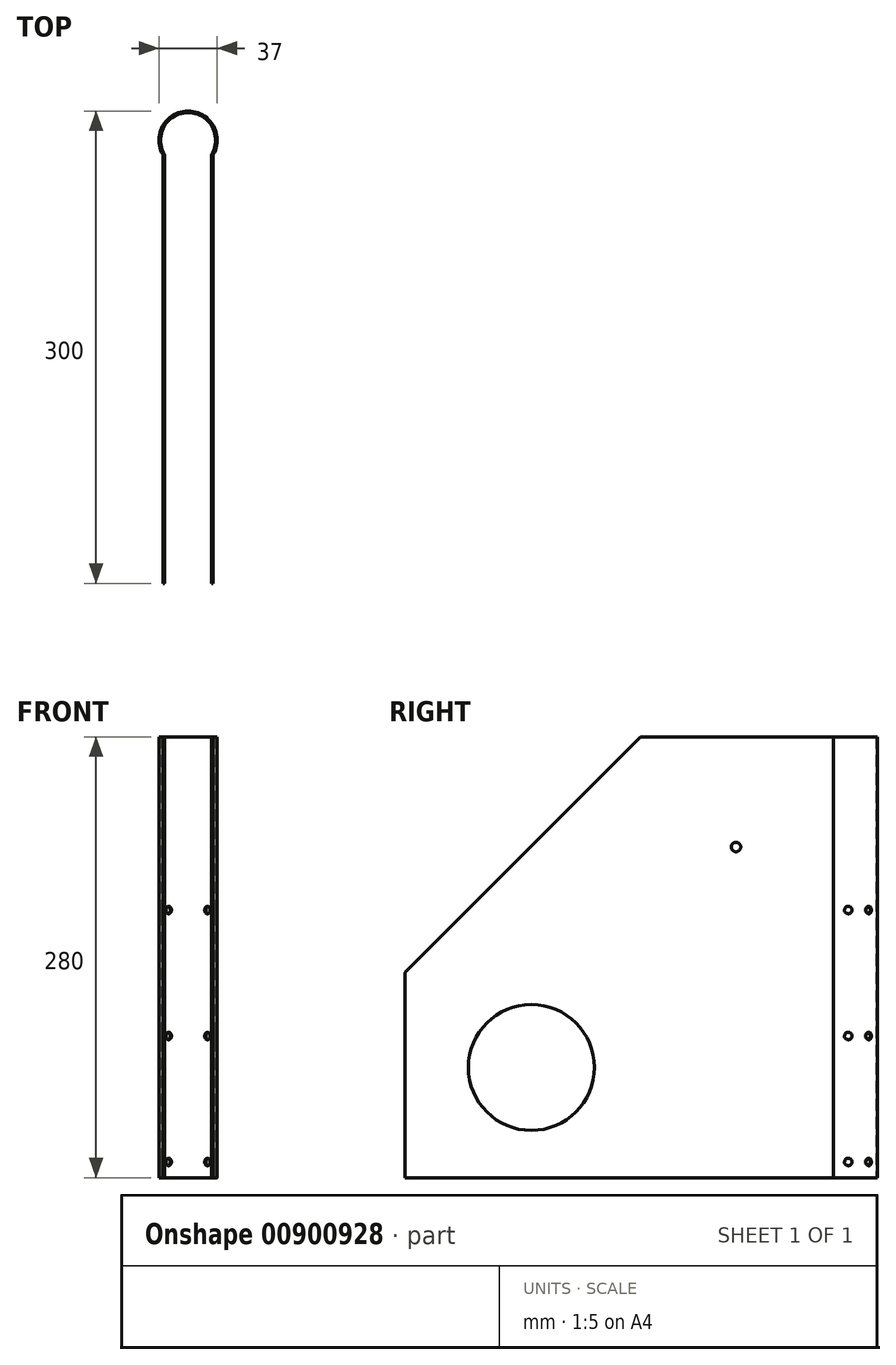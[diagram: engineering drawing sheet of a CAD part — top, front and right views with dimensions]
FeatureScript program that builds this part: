
annotation { "Feature Type Name" : "Feature", "Feature Type Description" : "" }
export const myFeature = defineFeature(function(context is Context, id is Id, definition is map)
    precondition{}
    {
        {
            var Q0;
            Q0=qCreatedBy(makeId("Top.planeOp"),FACE);
            var sketch = newSketch(context, id + "F0", { "sketchPlane" : qUnion([Q0])});
            skArc(sketch, "E0", {"start": v(15, -9.01) * mm, "mid": v(0, 17.5) * mm, "end": v(-15, -9.01) * mm});
            skLineSegment(sketch, "E1.left", {"start": v(15, -9.01) * mm, "end": v(15, -17.5) * mm});
            skLineSegment(sketch, "E1.right", {"start": v(-15, -9.01) * mm, "end": v(-15, -17.5) * mm});
            skLineSegment(sketch, "E2.top", {"start": v(-15, -282.5) * mm, "end": v(15, -282.5) * mm});
            skLineSegment(sketch, "E2.left", {"start": v(-15, -9.01) * mm, "end": v(-15, -282.5) * mm});
            skLineSegment(sketch, "E2.right", {"start": v(15, -9.01) * mm, "end": v(15, -282.5) * mm});
            skSolve(sketch);
        }
        {
            var Q0;
            Q0=qCreatedBy(makeId("Front.planeOp"),FACE);
            var Q1;
            Q1=qCreatedBy(makeId("Right.planeOp"),FACE);
            cPlane(context, id + "F1", {"entities" : qUnion([Q0, Q1]), "cplaneType" : CPlaneType.MID_PLANE, "offset" : 25 * mm, "width" : 150 * mm, "height" : 150 * mm});
        }
        {
            var Q0;
            Q0=qCreatedBy(makeId("Top.planeOp"),FACE);
            var sketch = newSketch(context, id + "F2", { "sketchPlane" : qUnion([Q0])});
            skLineSegment(sketch, "E3.left", {"start": v(-16, -9.29) * mm, "end": v(-16, -18.5) * mm});
            skLineSegment(sketch, "E3.right", {"start": v(16, -9.29) * mm, "end": v(16, -18.5) * mm});
            skPoint(sketch, "E3.middle", {"position": v(0, 0) * mm});
            skLineSegment(sketch, "E4.top", {"start": v(-16, -281.5) * mm, "end": v(16, -281.5) * mm});
            skLineSegment(sketch, "E4.left", {"start": v(-16, -18.5) * mm, "end": v(-16, -281.5) * mm});
            skLineSegment(sketch, "E4.right", {"start": v(16, -18.5) * mm, "end": v(16, -281.5) * mm});
            skArc(sketch, "E5", {"start": v(16, -9.29) * mm, "mid": v(0, 18.5) * mm, "end": v(-16, -9.29) * mm});
            skPoint(sketch, "E6.orphan", {"position": v(16, 18.5) * mm});
            skPoint(sketch, "E7.orphan", {"position": v(-16, 18.5) * mm});
            skSolve(sketch);
        }
        {
            var Q0;
            Q0 = qSketchRegion(id + "F2", true);
            extrude(context, id + "F3", {"entities" : qUnion([Q0]), "depth" : 280 * mm, "offsetDistance" : 25 * mm});
        }
        {
            var Q0;
            Q0 = qSketchRegion(id + "F0", true);
            extrude(context, id + "F4", {"entities" : qUnion([Q0]), "operationType" : NewBodyOperationType.REMOVE, "depth" : 280 * mm, "offsetDistance" : 25 * mm});
        }
        {
            var Q0;
            Q0=qCreatedBy(makeId("Right.planeOp"),FACE);
            var sketch = newSketch(context, id + "F5", { "sketchPlane" : qUnion([Q0])});
            skPoint(sketch, "E8.middle", {"position": v(0, 0) * mm});
            skCircle(sketch, "E9", {"center": v(0, 170) * mm, "radius": 2.4 * mm});
            skCircle(sketch, "E10", {"center": v(0, 90) * mm, "radius": 2.4 * mm});
            skCircle(sketch, "E11", {"center": v(0, 10) * mm, "radius": 2.4 * mm});
            skSolve(sketch);
        }
        {
            var Q0;
            Q0 = qSketchRegion(id + "F5", true);
            extrude(context, id + "F6", {"entities" : qUnion([Q0]), "operationType" : NewBodyOperationType.REMOVE, "endBound" : BoundingType.SYMMETRIC, "oppositeDirection" : true, "depth" : 37 * mm, "offsetDistance" : 25 * mm});
        }
        {
            var Q0;
            Q0=qCreatedBy(id+"F1.planeOp",FACE);
            var sketch = newSketch(context, id + "F7", { "sketchPlane" : qUnion([Q0])});
            skLineSegment(sketch, "E12.top", {"start": v(-2.4, 10) * mm, "end": v(2.4, 10) * mm});
            skLineSegment(sketch, "E13.bottom", {"start": v(2.4, 10) * mm, "end": v(-2.4, 10) * mm});
            skLineSegment(sketch, "E13.top", {"start": v(2.4, 90) * mm, "end": v(-2.4, 90) * mm});
            skLineSegment(sketch, "E14.top", {"start": v(2.4, 170) * mm, "end": v(-2.4, 170) * mm});
            skCircle(sketch, "E15", {"center": v(0, 170) * mm, "radius": 2.4 * mm});
            skCircle(sketch, "E16", {"center": v(0, 90) * mm, "radius": 2.4 * mm});
            skCircle(sketch, "E17", {"center": v(0, 10) * mm, "radius": 2.4 * mm});
            skSolve(sketch);
        }
        {
            var Q0;
            Q0 = qSketchRegion(id + "F7", true);
            extrude(context, id + "F8", {"entities" : qUnion([Q0]), "operationType" : NewBodyOperationType.REMOVE, "oppositeDirection" : true, "depth" : 25 * mm, "offsetDistance" : 25 * mm});
        }
        {
            var Q0;
            Q0=qCreatedBy(makeId("Right.planeOp"),FACE);
            var Q1;
            Q1=qCreatedBy(makeId("Front.planeOp"),FACE);
            cPlane(context, id + "F9", {"entities" : qUnion([Q0, Q1]), "cplaneType" : CPlaneType.MID_PLANE, "offset" : 25 * mm, "flipAlignment" : true, "width" : 150 * mm, "height" : 150 * mm});
        }
        {
            var Q0;
            Q0=qCreatedBy(id+"F9.planeOp",FACE);
            var sketch = newSketch(context, id + "F10", { "sketchPlane" : qUnion([Q0])});
            skCircle(sketch, "E18", {"center": v(0, 170) * mm, "radius": 2.4 * mm});
            skCircle(sketch, "E19", {"center": v(0, 90) * mm, "radius": 2.4 * mm});
            skCircle(sketch, "E20", {"center": v(0, 10) * mm, "radius": 2.4 * mm});
            skSolve(sketch);
        }
        {
            var Q0;
            Q0 = qSketchRegion(id + "F10", true);
            extrude(context, id + "F11", {"entities" : qUnion([Q0]), "operationType" : NewBodyOperationType.REMOVE, "oppositeDirection" : true, "depth" : 25 * mm, "offsetDistance" : 25 * mm});
        }
        {
            var Q0;
            Q0=qCreatedBy(makeId("Right.planeOp"),FACE);
            var sketch = newSketch(context, id + "F12", { "sketchPlane" : qUnion([Q0])});
            skCircle(sketch, "E21", {"center": v(-201.29, 70) * mm, "radius": 40 * mm});
            skLineSegment(sketch, "E22.bottom", {"start": v(-281.95, 280) * mm, "end": v(-131.95, 280) * mm});
            skLineSegment(sketch, "E22.left", {"start": v(-281.95, 280) * mm, "end": v(-281.95, 130) * mm});
            skLineSegment(sketch, "E23", {"start": v(-131.95, 280) * mm, "end": v(-281.95, 130) * mm});
            skCircle(sketch, "E24", {"center": v(-71.29, 210) * mm, "radius": 3 * mm});
            skSolve(sketch);
        }
        {
            var Q0;
            Q0 = qSketchRegion(id + "F12", true);
            extrude(context, id + "F13", {"entities" : qUnion([Q0]), "operationType" : NewBodyOperationType.REMOVE, "endBound" : BoundingType.SYMMETRIC, "depth" : 40 * mm, "offsetDistance" : 25 * mm});
        }
    });
